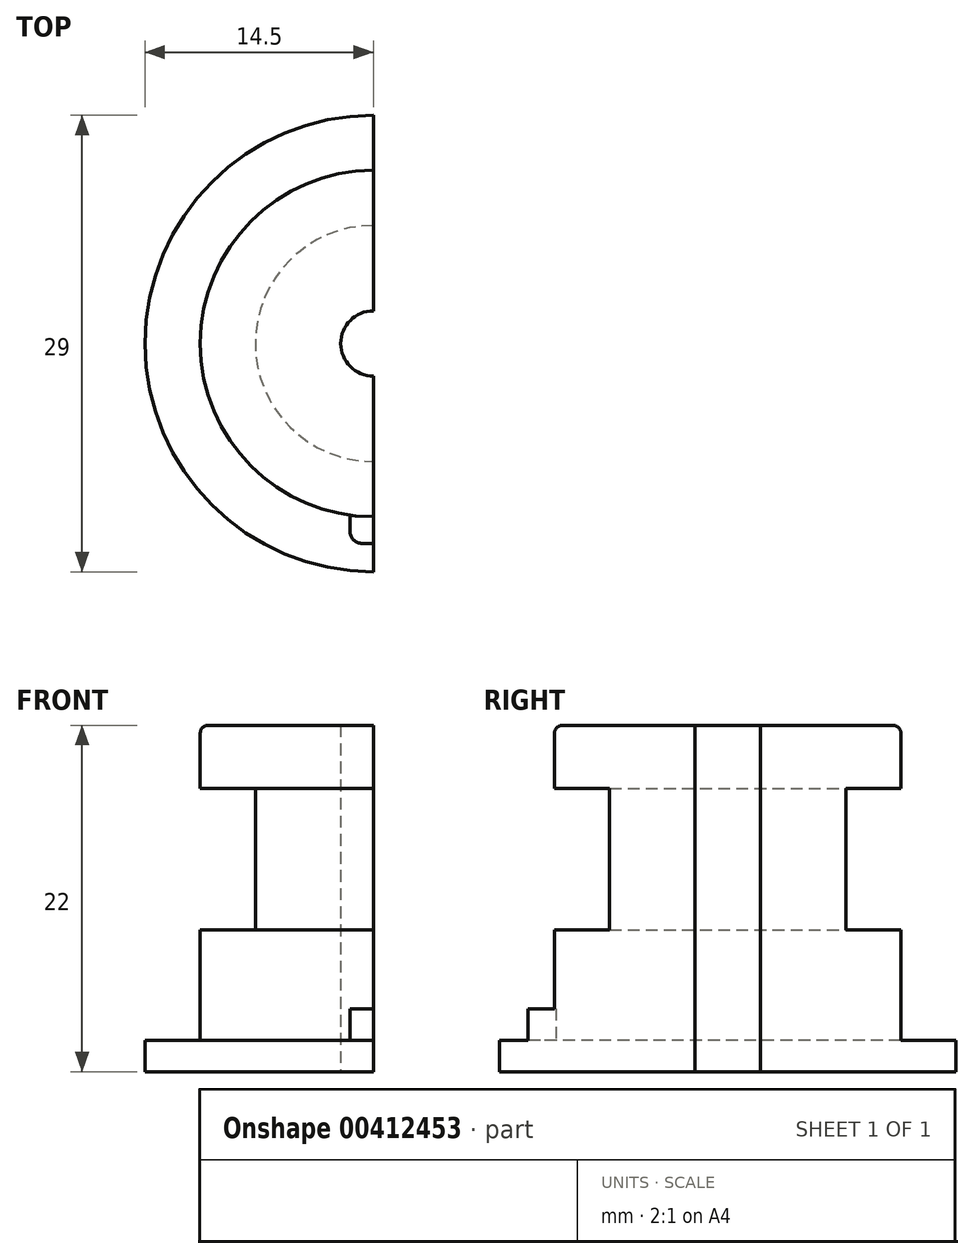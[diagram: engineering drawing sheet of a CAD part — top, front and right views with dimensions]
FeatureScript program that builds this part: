
annotation { "Feature Type Name" : "Feature", "Feature Type Description" : "" }
export const myFeature = defineFeature(function(context is Context, id is Id, definition is map)
    precondition{}
    {
        {
            var Q0;
            Q0=qCreatedBy(makeId("Top.planeOp"),FACE);
            var sketch = newSketch(context, id + "F0", { "sketchPlane" : qUnion([Q0])});
            skCircle(sketch, "E0", {"center": v(0, 0) * mm, "radius": 14.5 * mm});
            skSolve(sketch);
        }
        {
            var Q0;
            Q0=qSketchRegion(id+"F0",true);
            extrude(context, id + "F1", {"entities" : qUnion([Q0]), "depth" : 2 * mm});
        }
        {
            var Q0;
            Q0=makeQuery(id+"F1.opExtrude","CAP_FACE",FACE,{"disambiguationData":[OSD([sQuery(id+"F0.wireOp",EDGE,"E0")])],"isStart":false});
            var sketch = newSketch(context, id + "F2", { "sketchPlane" : qUnion([Q0])});
            skCircle(sketch, "E1", {"center": v(0, 0) * mm, "radius": 11 * mm});
            skSolve(sketch);
        }
        {
            var Q0;
            Q0=qSketchRegion(id+"F2",true);
            extrude(context, id + "F3", {"entities" : qUnion([Q0]), "operationType" : NewBodyOperationType.ADD, "depth" : 20 * mm});
        }
        {
            var Q0;
            Q0=makeQuery(id+"F1.opExtrude","CAP_FACE",FACE,{"disambiguationData":[OSD([sQuery(id+"F0.wireOp",EDGE,"E0")])],"isStart":true});
            var sketch = newSketch(context, id + "F4", { "sketchPlane" : qUnion([Q0])});
            skCircle(sketch, "E2", {"center": v(0, 0) * mm, "radius": 2.08 * mm});
            skSolve(sketch);
        }
        {
            var Q0;
            Q0=qSketchRegion(id+"F4",true);
            extrude(context, id + "F5", {"entities" : qUnion([Q0]), "operationType" : NewBodyOperationType.REMOVE, "endBound" : BoundingType.THROUGH_ALL, "oppositeDirection" : true, "depth" : 25 * mm});
        }
        {
            var Q0;
            Q0=makeQuery(id+"F1.opExtrude","CAP_FACE",FACE,{"disambiguationData":[OSD([sQuery(id+"F0.wireOp",EDGE,"E0")])],"isStart":false});
            var sketch = newSketch(context, id + "F6", { "sketchPlane" : qUnion([Q0])});
            skLineSegment(sketch, "E3.bottom", {"start": v(-1.5, -9.3) * mm, "end": v(1.5, -9.3) * mm});
            skLineSegment(sketch, "E3.top", {"start": v(-1.5, -12.7) * mm, "end": v(1.5, -12.7) * mm});
            skLineSegment(sketch, "E3.left", {"start": v(-1.5, -9.3) * mm, "end": v(-1.5, -12.7) * mm});
            skLineSegment(sketch, "E3.right", {"start": v(1.5, -9.3) * mm, "end": v(1.5, -12.7) * mm});
            skPoint(sketch, "E3.middle", {"position": v(0, -11) * mm});
            skSolve(sketch);
        }
        {
            var Q0;
            {var subQ0=sQuery(id+"F6.wireOp",EDGE,"E3.top");Q0=makeQuery(id+"F6.imprint","IMPRINT",FACE,{"disambiguationData":[TD([[makeQuery(id+"F6.imprint","IMPRINT",EDGE,{"derivedFrom":subQ0}),1.0]])]});}
            extrude(context, id + "F7", {"entities" : qUnion([Q0]), "operationType" : NewBodyOperationType.ADD, "depth" : 2 * mm});
        }
        {
            var Q0;
            Q0=makeQuery(id+"F7.opExtrude","SWEPT_EDGE",EDGE,{"disambiguationData":[OSD([sQuery(id+"F6.wireOp",EDGE,"E3.top"),sQuery(id+"F6.wireOp",EDGE,"E3.left")])]});
            var Q1;
            Q1=makeQuery(id+"F7.opExtrude","SWEPT_EDGE",EDGE,{"disambiguationData":[OSD([sQuery(id+"F6.wireOp",EDGE,"E3.top"),sQuery(id+"F6.wireOp",EDGE,"E3.right")])]});
            fillet(context, id + "F8", {"entities" : qUnion([Q0, Q1]), "radius" : 0.8 * mm, "tangentPropagation" : true, "allowEdgeOverflow" : false});
        }
        {
            var Q0;
            Q0=makeQuery(id+"F3.opExtrude","CAP_EDGE",EDGE,{"disambiguationData":[OSD([sQuery(id+"F2.wireOp",EDGE,"E1")])],"isStart":false});
            fillet(context, id + "F9", {"entities" : qUnion([Q0]), "radius" : 0.5 * mm, "tangentPropagation" : true, "allowEdgeOverflow" : false});
        }
        {
            var Q0;
            Q0=qCreatedBy(makeId("Top.planeOp"),FACE);
            var sketch = newSketch(context, id + "F10", { "sketchPlane" : qUnion([Q0])});
            skLineSegment(sketch, "E4.bottom", {"start": v(0, 35.14) * mm, "end": v(27.06, 35.14) * mm});
            skLineSegment(sketch, "E4.top", {"start": v(0, -35.78) * mm, "end": v(27.06, -35.78) * mm});
            skLineSegment(sketch, "E4.left", {"start": v(0, 35.14) * mm, "end": v(0, -35.78) * mm});
            skLineSegment(sketch, "E4.right", {"start": v(27.06, 35.14) * mm, "end": v(27.06, -35.78) * mm});
            skSolve(sketch);
        }
        {
            var Q0;
            Q0=qSketchRegion(id+"F10",true);
            extrude(context, id + "F11", {"entities" : qUnion([Q0]), "operationType" : NewBodyOperationType.REMOVE, "endBound" : BoundingType.THROUGH_ALL, "depth" : 25 * mm});
        }
        {
            var Q0;
            Q0=qCreatedBy(makeId("Right.planeOp"),FACE);
            var sketch = newSketch(context, id + "F12", { "sketchPlane" : qUnion([Q0])});
            skLineSegment(sketch, "E5", {"start": v(0, 0) * mm, "end": v(0, 26.62) * mm});
            skSolve(sketch);
        }
        {
            var Q0;
            Q0=qCreatedBy(makeId("Front.planeOp"),FACE);
            var sketch = newSketch(context, id + "F13", { "sketchPlane" : qUnion([Q0])});
            skLineSegment(sketch, "E6.bottom", {"start": v(11, 18) * mm, "end": v(7.5, 18) * mm});
            skLineSegment(sketch, "E6.top", {"start": v(11, 9) * mm, "end": v(7.5, 9) * mm});
            skLineSegment(sketch, "E6.left", {"start": v(11, 18) * mm, "end": v(11, 9) * mm});
            skLineSegment(sketch, "E6.right", {"start": v(7.5, 18) * mm, "end": v(7.5, 9) * mm});
            skSolve(sketch);
        }
        {
            var Q0;
            Q0=qSketchRegion(id+"F13",true);
            var Q1;
            Q1=sQuery(id+"F12.wireOp",EDGE,"E5");
            revolve(context, id + "F14", {"operationType" : NewBodyOperationType.REMOVE, "entities" : qUnion([Q0]), "axis" : qUnion([Q1]), "revolveType" : RevolveType.FULL});
        }
    });
